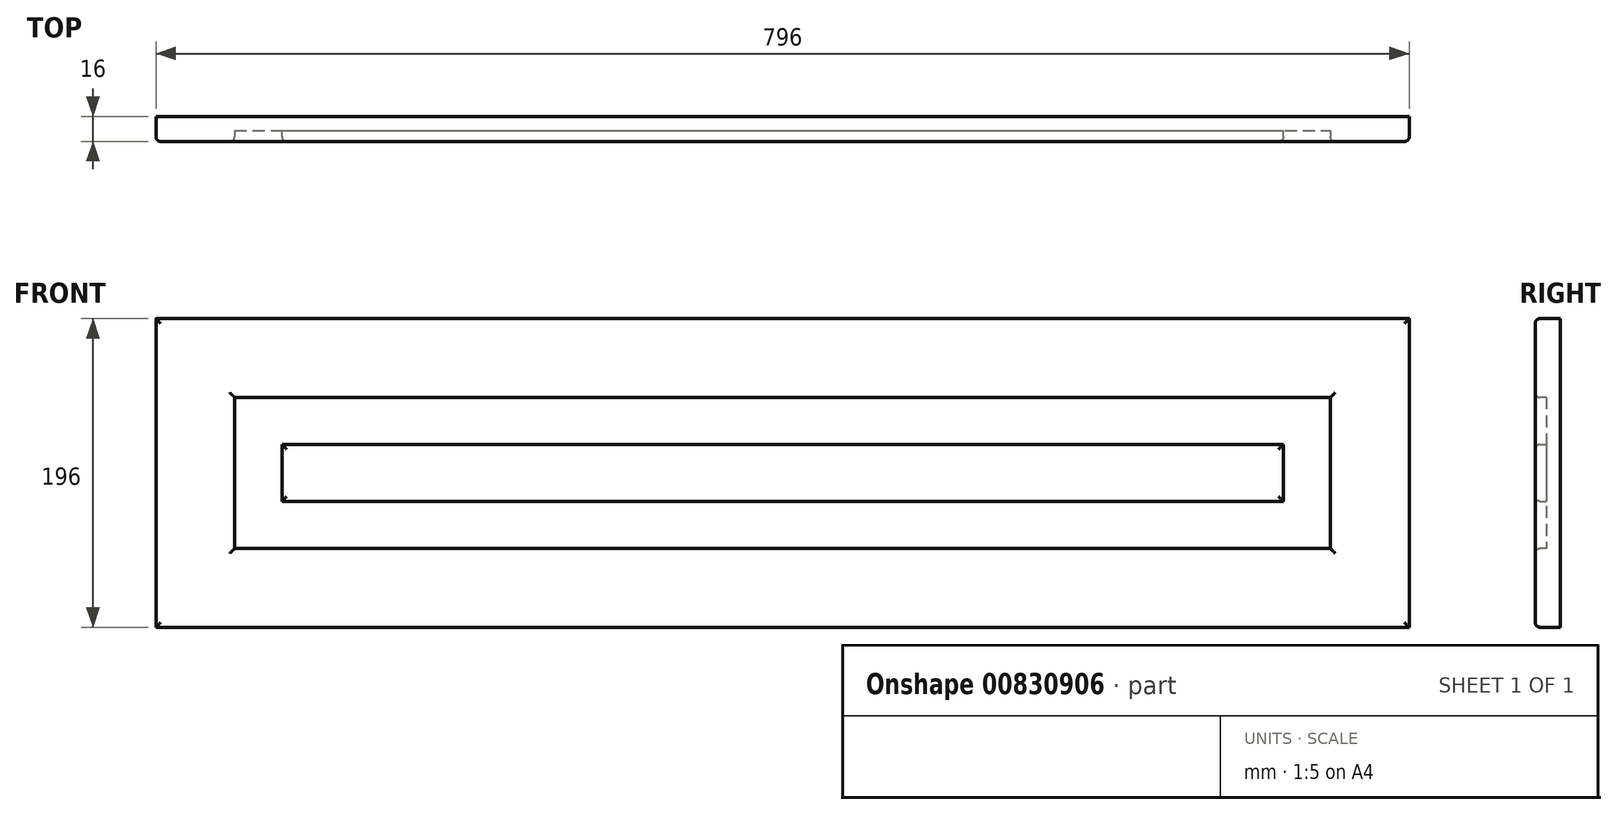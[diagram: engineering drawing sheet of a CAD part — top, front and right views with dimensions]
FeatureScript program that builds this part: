
annotation { "Feature Type Name" : "Feature", "Feature Type Description" : "" }
export const myFeature = defineFeature(function(context is Context, id is Id, definition is map)
    precondition{}
    {
        {
            var Q0;
            Q0=qCreatedBy(makeId("Front.planeOp"),FACE);
            var sketch = newSketch(context, id + "F0", { "sketchPlane" : qUnion([Q0])});
            skLineSegment(sketch, "E0.bottom", {"start": v(0, 0) * mm, "end": v(44.66, 0) * mm});
            skLineSegment(sketch, "E0.top", {"start": v(0, 33.8) * mm, "end": v(44.66, 33.8) * mm});
            skLineSegment(sketch, "E0.left", {"start": v(0, 0) * mm, "end": v(0, 33.8) * mm});
            skLineSegment(sketch, "E0.right", {"start": v(44.66, 0) * mm, "end": v(44.66, 33.8) * mm});
            skSolve(sketch);
        }
        {
            var Q0;
            Q0=makeQuery(id+"F0.imprint","IMPRINT",FACE,{"disambiguationData":[TD([[makeQuery(id+"F0.imprint","IMPRINT",EDGE,{"derivedFrom":sQuery(id+"F0.wireOp",EDGE,"E0.bottom")}),1.0]])]});
            extrude(context, id + "F1", {"entities" : qUnion([Q0]), "depth" : 16 * mm, "offsetDistance" : 25.4 * mm});
        }
        {
            var Q0;
            Q0=makeQuery(id+"F1.opExtrude","SWEPT_FACE",FACE,{"disambiguationData":[OSD([sQuery(id+"F0.wireOp",EDGE,"E0.bottom")])]});
            extrude(context, id + "F2", {"entities" : qUnion([Q0]), "operationType" : NewBodyOperationType.ADD, "oppositeDirection" : true, "depth" : 796 * mm, "offsetDistance" : 25 * mm});
        }
        {
            var Q0;
            {var subQ0=sQuery(id+"F0.wireOp",EDGE,"E0.left");Q0=makeQuery(id+"F2.boolean.opBoolean","MERGE",FACE,{"derivedFrom":[makeQuery(id+"F1.opExtrude","SWEPT_FACE",FACE,{"disambiguationData":[OSD([subQ0])]}),makeQuery(id+"F2.opExtrude","SWEPT_FACE",FACE,{"disambiguationData":[OSD([sQuery(id+"F0.wireOp",EDGE,"E0.bottom"),subQ0])]})]});}
            extrude(context, id + "F3", {"entities" : qUnion([Q0]), "operationType" : NewBodyOperationType.ADD, "oppositeDirection" : true, "depth" : 196 * mm, "offsetDistance" : 25 * mm});
        }
        {
            var Q0;
            {var subQ0=sQuery(id+"F0.wireOp",EDGE,"E0.left");var subQ1=sQuery(id+"F0.wireOp",EDGE,"E0.bottom");Q0=makeQuery(id+"F3.boolean.opBoolean","MERGE",FACE,{"derivedFrom":[makeQuery(id+"F2.boolean.opBoolean","MERGE",FACE,{"derivedFrom":[makeQuery(id+"F1.opExtrude","CAP_FACE",FACE,{"disambiguationData":[OSD([subQ1,sQuery(id+"F0.wireOp",EDGE,"E0.top"),subQ0,sQuery(id+"F0.wireOp",EDGE,"E0.right")])],"isStart":false}),makeQuery(id+"F2.opExtrude","SWEPT_FACE",FACE,{"disambiguationData":[OSD([subQ1]),TDD([makeQuery(id+"F1.opExtrude","CAP_EDGE",EDGE,{"disambiguationData":[OSD([subQ1])],"isStart":false})])]})]}),makeQuery(id+"F3.opExtrude","SWEPT_FACE",FACE,{"disambiguationData":[OSD([subQ1,subQ0]),TDD([makeQuery(id+"F2.boolean.opBoolean","MERGE",EDGE,{"derivedFrom":[makeQuery(id+"F1.opExtrude","CAP_EDGE",EDGE,{"disambiguationData":[OSD([subQ0])],"isStart":false}),makeQuery(id+"F2.opExtrude","SWEPT_EDGE",EDGE,{"disambiguationData":[OSD([subQ1,subQ0]),TDD([makeQuery(id+"F1.opExtrude","CAP_VERTEX",VERTEX,{"disambiguationData":[OSD([subQ1,subQ0])],"isStart":false})])]})]})])]})]});}
            var sketch = newSketch(context, id + "F4", { "sketchPlane" : qUnion([Q0])});
            skLineSegment(sketch, "E1.bottom", {"start": v(59.7, 646.67) * mm, "end": v(128.66, 646.67) * mm});
            skLineSegment(sketch, "E1.top", {"start": v(59.7, 152.97) * mm, "end": v(128.66, 152.97) * mm});
            skLineSegment(sketch, "E1.left", {"start": v(59.7, 646.67) * mm, "end": v(59.7, 152.97) * mm});
            skLineSegment(sketch, "E1.right", {"start": v(128.66, 646.67) * mm, "end": v(128.66, 152.97) * mm});
            skSolve(sketch);
        }
        {
            var Q0;
            Q0=makeQuery(id+"F4.imprint","IMPRINT",FACE,{"disambiguationData":[TD([[makeQuery(id+"F4.imprint","IMPRINT",EDGE,{"derivedFrom":sQuery(id+"F4.wireOp",EDGE,"E1.bottom")}),-1.0]])]});
            extrude(context, id + "F5", {"entities" : qUnion([Q0]), "operationType" : NewBodyOperationType.REMOVE, "oppositeDirection" : true, "depth" : 7 * mm, "offsetDistance" : 25 * mm});
        }
        {
            var Q0;
            Q0=makeQuery(id+"F5.boolean.opBoolean","COPY",FACE,{"derivedFrom":makeQuery(id+"F5.opExtrude","SWEPT_FACE",FACE,{"disambiguationData":[OSD([sQuery(id+"F4.wireOp",EDGE,"E1.left")])]})});
            extrude(context, id + "F6", {"entities" : qUnion([Q0]), "operationType" : NewBodyOperationType.REMOVE, "oppositeDirection" : true, "depth" : 9.7 * mm, "offsetDistance" : 25 * mm});
        }
        {
            var Q0;
            {var subQ0=sQuery(id+"F4.wireOp",EDGE,"E1.bottom");Q0=makeQuery(id+"F6.boolean.opBoolean","MERGE",FACE,{"derivedFrom":[makeQuery(id+"F5.boolean.opBoolean","COPY",FACE,{"derivedFrom":makeQuery(id+"F5.opExtrude","SWEPT_FACE",FACE,{"disambiguationData":[OSD([subQ0])]})}),makeQuery(id+"F6.opExtrude","SWEPT_FACE",FACE,{"disambiguationData":[OSD([subQ0,sQuery(id+"F4.wireOp",EDGE,"E1.left")])]})]});}
            extrude(context, id + "F7", {"entities" : qUnion([Q0]), "operationType" : NewBodyOperationType.ADD, "oppositeDirection" : true, "depth" : 99.33 * mm, "offsetDistance" : 25 * mm});
        }
        {
            var Q0;
            {var subQ0=sQuery(id+"F4.wireOp",EDGE,"E1.bottom");Q0=makeQuery(id+"F6.boolean.opBoolean","MERGE",FACE,{"derivedFrom":[makeQuery(id+"F5.boolean.opBoolean","COPY",FACE,{"derivedFrom":makeQuery(id+"F5.opExtrude","SWEPT_FACE",FACE,{"disambiguationData":[OSD([subQ0])]})}),makeQuery(id+"F6.opExtrude","SWEPT_FACE",FACE,{"disambiguationData":[OSD([subQ0,sQuery(id+"F4.wireOp",EDGE,"E1.left")])]})]});}
            extrude(context, id + "F8", {"entities" : qUnion([Q0]), "operationType" : NewBodyOperationType.REMOVE, "oppositeDirection" : true, "depth" : 99.33 * mm, "offsetDistance" : 25 * mm});
        }
        {
            var Q0;
            {var subQ0=sQuery(id+"F4.wireOp",EDGE,"E1.right");Q0=makeQuery(id+"F8.boolean.opBoolean","MERGE",FACE,{"derivedFrom":[makeQuery(id+"F5.boolean.opBoolean","COPY",FACE,{"derivedFrom":makeQuery(id+"F5.opExtrude","SWEPT_FACE",FACE,{"disambiguationData":[OSD([subQ0])]})}),makeQuery(id+"F8.opExtrude","SWEPT_FACE",FACE,{"disambiguationData":[OSD([sQuery(id+"F4.wireOp",EDGE,"E1.bottom"),subQ0])]})]});}
            extrude(context, id + "F9", {"entities" : qUnion([Q0]), "operationType" : NewBodyOperationType.REMOVE, "oppositeDirection" : true, "depth" : 17.34 * mm, "offsetDistance" : 25 * mm});
        }
        {
            var Q0;
            {var subQ0=sQuery(id+"F4.wireOp",EDGE,"E1.top");Q0=makeQuery(id+"F9.boolean.opBoolean","MERGE",FACE,{"derivedFrom":[makeQuery(id+"F6.boolean.opBoolean","MERGE",FACE,{"derivedFrom":[makeQuery(id+"F5.boolean.opBoolean","COPY",FACE,{"derivedFrom":makeQuery(id+"F5.opExtrude","SWEPT_FACE",FACE,{"disambiguationData":[OSD([subQ0])]})}),makeQuery(id+"F6.opExtrude","SWEPT_FACE",FACE,{"disambiguationData":[OSD([subQ0,sQuery(id+"F4.wireOp",EDGE,"E1.left")])]})]}),makeQuery(id+"F9.opExtrude","SWEPT_FACE",FACE,{"disambiguationData":[OSD([subQ0,sQuery(id+"F4.wireOp",EDGE,"E1.right")])]})]});}
            extrude(context, id + "F10", {"entities" : qUnion([Q0]), "operationType" : NewBodyOperationType.REMOVE, "oppositeDirection" : true, "depth" : 102.97 * mm, "offsetDistance" : 25 * mm});
        }
        {
            var Q0;
            {var subQ0=sQuery(id+"F4.wireOp",EDGE,"E1.right");var subQ1=sQuery(id+"F4.wireOp",EDGE,"E1.top");var subQ2=sQuery(id+"F4.wireOp",EDGE,"E1.left");var subQ3=sQuery(id+"F4.wireOp",EDGE,"E1.bottom");Q0=makeQuery(id+"F10.boolean.opBoolean","MERGE",FACE,{"derivedFrom":[makeQuery(id+"F9.boolean.opBoolean","MERGE",FACE,{"derivedFrom":[makeQuery(id+"F8.boolean.opBoolean","MERGE",FACE,{"derivedFrom":[makeQuery(id+"F6.boolean.opBoolean","MERGE",FACE,{"derivedFrom":[makeQuery(id+"F5.boolean.opBoolean","COPY",FACE,{"derivedFrom":makeQuery(id+"F5.opExtrude","CAP_FACE",FACE,{"disambiguationData":[OSD([subQ3,subQ1,subQ2,subQ0])],"isStart":false})}),makeQuery(id+"F6.opExtrude","SWEPT_FACE",FACE,{"disambiguationData":[OSD([subQ2]),TDD([makeQuery(id+"F5.boolean.opBoolean","COPY",EDGE,{"derivedFrom":makeQuery(id+"F5.opExtrude","CAP_EDGE",EDGE,{"disambiguationData":[OSD([subQ2])],"isStart":false})})])]})]}),makeQuery(id+"F8.opExtrude","SWEPT_FACE",FACE,{"disambiguationData":[OSD([subQ3,subQ2]),TDD([makeQuery(id+"F6.boolean.opBoolean","MERGE",EDGE,{"derivedFrom":[makeQuery(id+"F5.boolean.opBoolean","COPY",EDGE,{"derivedFrom":makeQuery(id+"F5.opExtrude","CAP_EDGE",EDGE,{"disambiguationData":[OSD([subQ3])],"isStart":false})}),makeQuery(id+"F6.opExtrude","SWEPT_EDGE",EDGE,{"disambiguationData":[OSD([subQ3,subQ2]),TDD([makeQuery(id+"F5.boolean.opBoolean","COPY",VERTEX,{"derivedFrom":makeQuery(id+"F5.opExtrude","CAP_VERTEX",VERTEX,{"disambiguationData":[OSD([subQ3,subQ2])],"isStart":false})})])]})]})])]})]}),makeQuery(id+"F9.opExtrude","SWEPT_FACE",FACE,{"disambiguationData":[OSD([subQ3,subQ0]),TDD([makeQuery(id+"F8.boolean.opBoolean","MERGE",EDGE,{"derivedFrom":[makeQuery(id+"F5.boolean.opBoolean","COPY",EDGE,{"derivedFrom":makeQuery(id+"F5.opExtrude","CAP_EDGE",EDGE,{"disambiguationData":[OSD([subQ0])],"isStart":false})}),makeQuery(id+"F8.opExtrude","SWEPT_EDGE",EDGE,{"disambiguationData":[OSD([subQ3,subQ0]),TDD([makeQuery(id+"F5.boolean.opBoolean","COPY",VERTEX,{"derivedFrom":makeQuery(id+"F5.opExtrude","CAP_VERTEX",VERTEX,{"disambiguationData":[OSD([subQ3,subQ0])],"isStart":false})})])]})]})])]})]}),makeQuery(id+"F10.opExtrude","SWEPT_FACE",FACE,{"disambiguationData":[OSD([subQ1,subQ2,subQ0]),TDD([makeQuery(id+"F9.boolean.opBoolean","MERGE",EDGE,{"derivedFrom":[makeQuery(id+"F6.boolean.opBoolean","MERGE",EDGE,{"derivedFrom":[makeQuery(id+"F5.boolean.opBoolean","COPY",EDGE,{"derivedFrom":makeQuery(id+"F5.opExtrude","CAP_EDGE",EDGE,{"disambiguationData":[OSD([subQ1])],"isStart":false})}),makeQuery(id+"F6.opExtrude","SWEPT_EDGE",EDGE,{"disambiguationData":[OSD([subQ1,subQ2]),TDD([makeQuery(id+"F5.boolean.opBoolean","COPY",VERTEX,{"derivedFrom":makeQuery(id+"F5.opExtrude","CAP_VERTEX",VERTEX,{"disambiguationData":[OSD([subQ1,subQ2])],"isStart":false})})])]})]}),makeQuery(id+"F9.opExtrude","SWEPT_EDGE",EDGE,{"disambiguationData":[OSD([subQ1,subQ0]),TDD([makeQuery(id+"F5.boolean.opBoolean","COPY",VERTEX,{"derivedFrom":makeQuery(id+"F5.opExtrude","CAP_VERTEX",VERTEX,{"disambiguationData":[OSD([subQ1,subQ0])],"isStart":false})})])]})]})])]})]});}
            var sketch = newSketch(context, id + "F11", { "sketchPlane" : qUnion([Q0])});
            skLineSegment(sketch, "E2.bottom", {"start": v(74.13, 678.73) * mm, "end": v(109.41, 678.73) * mm});
            skLineSegment(sketch, "E2.top", {"start": v(74.13, 186.63) * mm, "end": v(109.41, 186.63) * mm});
            skLineSegment(sketch, "E2.left", {"start": v(74.13, 678.73) * mm, "end": v(74.13, 186.63) * mm});
            skLineSegment(sketch, "E2.right", {"start": v(109.41, 678.73) * mm, "end": v(109.41, 186.63) * mm});
            skSolve(sketch);
        }
        {
            var Q0;
            Q0=makeQuery(id+"F11.imprint","IMPRINT",FACE,{"disambiguationData":[TD([[makeQuery(id+"F11.imprint","IMPRINT",EDGE,{"derivedFrom":sQuery(id+"F11.wireOp",EDGE,"E2.bottom")}),-1.0]])]});
            extrude(context, id + "F12", {"entities" : qUnion([Q0]), "operationType" : NewBodyOperationType.ADD, "depth" : 7 * mm, "offsetDistance" : 25 * mm});
        }
        {
            var Q0;
            Q0=makeQuery(id+"F12.opExtrude","SWEPT_FACE",FACE,{"disambiguationData":[OSD([sQuery(id+"F11.wireOp",EDGE,"E2.bottom")])]});
            extrude(context, id + "F13", {"entities" : qUnion([Q0]), "operationType" : NewBodyOperationType.ADD, "depth" : 37.27 * mm, "offsetDistance" : 25 * mm});
        }
        {
            var Q0;
            {var subQ0=sQuery(id+"F11.wireOp",EDGE,"E2.right");Q0=makeQuery(id+"F13.boolean.opBoolean","MERGE",FACE,{"derivedFrom":[makeQuery(id+"F12.opExtrude","SWEPT_FACE",FACE,{"disambiguationData":[OSD([subQ0])]}),makeQuery(id+"F13.opExtrude","SWEPT_FACE",FACE,{"disambiguationData":[OSD([sQuery(id+"F11.wireOp",EDGE,"E2.bottom"),subQ0])]})]});}
            extrude(context, id + "F14", {"entities" : qUnion([Q0]), "operationType" : NewBodyOperationType.ADD, "depth" : 6.58 * mm, "offsetDistance" : 25 * mm});
        }
        {
            var Q0;
            {var subQ0=sQuery(id+"F11.wireOp",EDGE,"E2.top");Q0=makeQuery(id+"F14.boolean.opBoolean","MERGE",FACE,{"derivedFrom":[makeQuery(id+"F12.opExtrude","SWEPT_FACE",FACE,{"disambiguationData":[OSD([subQ0])]}),makeQuery(id+"F14.opExtrude","SWEPT_FACE",FACE,{"disambiguationData":[OSD([subQ0,sQuery(id+"F11.wireOp",EDGE,"E2.right")])]})]});}
            extrude(context, id + "F15", {"entities" : qUnion([Q0]), "operationType" : NewBodyOperationType.ADD, "depth" : 106.63 * mm, "offsetDistance" : 25 * mm});
        }
        {
            var Q0;
            {var subQ0=sQuery(id+"F11.wireOp",EDGE,"E2.left");Q0=makeQuery(id+"F15.boolean.opBoolean","MERGE",FACE,{"derivedFrom":[makeQuery(id+"F13.boolean.opBoolean","MERGE",FACE,{"derivedFrom":[makeQuery(id+"F12.opExtrude","SWEPT_FACE",FACE,{"disambiguationData":[OSD([subQ0])]}),makeQuery(id+"F13.opExtrude","SWEPT_FACE",FACE,{"disambiguationData":[OSD([sQuery(id+"F11.wireOp",EDGE,"E2.bottom"),subQ0])]})]}),makeQuery(id+"F15.opExtrude","SWEPT_FACE",FACE,{"disambiguationData":[OSD([sQuery(id+"F11.wireOp",EDGE,"E2.top"),subQ0])]})]});}
            extrude(context, id + "F16", {"entities" : qUnion([Q0]), "operationType" : NewBodyOperationType.REMOVE, "oppositeDirection" : true, "depth" : 5.87 * mm, "offsetDistance" : 25 * mm});
        }
        {
            var Q0;
            Q0=makeQuery(id+"F3.opExtrude","CAP_FACE",FACE,{"disambiguationData":[OSD([sQuery(id+"F0.wireOp",EDGE,"E0.bottom"),sQuery(id+"F0.wireOp",EDGE,"E0.left")])],"isStart":false});
            extrude(context, id + "F17", {"entities" : qUnion([Q0]), "operationType" : NewBodyOperationType.ADD, "depth" : 200 * mm, "offsetDistance" : 25 * mm});
        }
        {
            var Q0;
            {var subQ0=sQuery(id+"F4.wireOp",EDGE,"E1.right");Q0=makeQuery(id+"F10.boolean.opBoolean","MERGE",FACE,{"derivedFrom":[makeQuery(id+"F9.boolean.opBoolean","COPY",FACE,{"derivedFrom":makeQuery(id+"F9.opExtrude","CAP_FACE",FACE,{"disambiguationData":[OSD([sQuery(id+"F4.wireOp",EDGE,"E1.bottom"),subQ0])],"isStart":false})}),makeQuery(id+"F10.opExtrude","SWEPT_FACE",FACE,{"disambiguationData":[OSD([sQuery(id+"F4.wireOp",EDGE,"E1.top"),subQ0])]})]});}
            extrude(context, id + "F18", {"entities" : qUnion([Q0]), "operationType" : NewBodyOperationType.REMOVE, "oppositeDirection" : true, "depth" : 200 * mm, "offsetDistance" : 25 * mm});
        }
        {
            var Q0;
            {var subQ0=sQuery(id+"F11.wireOp",EDGE,"E2.right");var subQ1=sQuery(id+"F11.wireOp",EDGE,"E2.top");Q0=makeQuery(id+"F15.boolean.opBoolean","MERGE",FACE,{"derivedFrom":[makeQuery(id+"F14.opExtrude","CAP_FACE",FACE,{"disambiguationData":[OSD([sQuery(id+"F11.wireOp",EDGE,"E2.bottom"),subQ0])],"isStart":false}),makeQuery(id+"F15.opExtrude","SWEPT_FACE",FACE,{"disambiguationData":[OSD([subQ1,subQ0]),TDD([makeQuery(id+"F14.opExtrude","CAP_EDGE",EDGE,{"disambiguationData":[OSD([subQ1,subQ0])],"isStart":false})])]})]});}
            extrude(context, id + "F19", {"entities" : qUnion([Q0]), "operationType" : NewBodyOperationType.ADD, "depth" : 200 * mm, "offsetDistance" : 25 * mm});
        }
        {
            var Q0;
            Q0=makeQuery(id+"F17.opExtrude","CAP_FACE",FACE,{"disambiguationData":[OSD([sQuery(id+"F0.wireOp",EDGE,"E0.bottom"),sQuery(id+"F0.wireOp",EDGE,"E0.left")])],"isStart":false});
            extrude(context, id + "F20", {"entities" : qUnion([Q0]), "operationType" : NewBodyOperationType.ADD, "depth" : 200 * mm, "offsetDistance" : 25 * mm});
        }
        {
            var Q0;
            Q0=makeQuery(id+"F18.boolean.opBoolean","COPY",FACE,{"derivedFrom":makeQuery(id+"F18.opExtrude","CAP_FACE",FACE,{"disambiguationData":[OSD([sQuery(id+"F4.wireOp",EDGE,"E1.bottom"),sQuery(id+"F4.wireOp",EDGE,"E1.top"),sQuery(id+"F4.wireOp",EDGE,"E1.right")])],"isStart":false})});
            extrude(context, id + "F21", {"entities" : qUnion([Q0]), "operationType" : NewBodyOperationType.REMOVE, "oppositeDirection" : true, "depth" : 200 * mm, "offsetDistance" : 25 * mm});
        }
        {
            var Q0;
            Q0=makeQuery(id+"F19.opExtrude","CAP_FACE",FACE,{"disambiguationData":[OSD([sQuery(id+"F11.wireOp",EDGE,"E2.bottom"),sQuery(id+"F11.wireOp",EDGE,"E2.top"),sQuery(id+"F11.wireOp",EDGE,"E2.right")])],"isStart":false});
            extrude(context, id + "F22", {"entities" : qUnion([Q0]), "operationType" : NewBodyOperationType.ADD, "depth" : 200 * mm, "offsetDistance" : 25 * mm});
        }
        {
            var Q0;
            {var subQ0=sQuery(id+"F11.wireOp",EDGE,"E2.right");var subQ1=sQuery(id+"F11.wireOp",EDGE,"E2.top");Q0=makeQuery(id+"F22.boolean.opBoolean","MERGE",FACE,{"derivedFrom":[makeQuery(id+"F19.boolean.opBoolean","MERGE",FACE,{"derivedFrom":[makeQuery(id+"F15.opExtrude","CAP_FACE",FACE,{"disambiguationData":[OSD([subQ1,subQ0])],"isStart":false}),makeQuery(id+"F19.opExtrude","SWEPT_FACE",FACE,{"disambiguationData":[OSD([subQ1,subQ0])]})]}),makeQuery(id+"F22.opExtrude","SWEPT_FACE",FACE,{"disambiguationData":[OSD([subQ1,subQ0])]})]});}
            extrude(context, id + "F23", {"entities" : qUnion([Q0]), "operationType" : NewBodyOperationType.REMOVE, "oppositeDirection" : true, "depth" : 600 * mm, "offsetDistance" : 25 * mm});
        }
        {
            var Q0;
            {var subQ0=sQuery(id+"F4.wireOp",EDGE,"E1.right");var subQ1=sQuery(id+"F4.wireOp",EDGE,"E1.top");Q0=makeQuery(id+"F21.boolean.opBoolean","MERGE",FACE,{"derivedFrom":[makeQuery(id+"F18.boolean.opBoolean","MERGE",FACE,{"derivedFrom":[makeQuery(id+"F10.boolean.opBoolean","COPY",FACE,{"derivedFrom":makeQuery(id+"F10.opExtrude","CAP_FACE",FACE,{"disambiguationData":[OSD([subQ1,sQuery(id+"F4.wireOp",EDGE,"E1.left"),subQ0])],"isStart":false})}),makeQuery(id+"F18.opExtrude","SWEPT_FACE",FACE,{"disambiguationData":[OSD([subQ1,subQ0])]})]}),makeQuery(id+"F21.opExtrude","SWEPT_FACE",FACE,{"disambiguationData":[OSD([subQ1,subQ0])]})]});}
            extrude(context, id + "F24", {"entities" : qUnion([Q0]), "operationType" : NewBodyOperationType.ADD, "depth" : 600 * mm, "offsetDistance" : 25 * mm});
        }
        {
            var Q0;
            {var subQ0=sQuery(id+"F0.wireOp",EDGE,"E0.left");var subQ1=sQuery(id+"F0.wireOp",EDGE,"E0.bottom");var subQ2=makeQuery(id+"F1.opExtrude","SWEPT_EDGE",EDGE,{"disambiguationData":[OSD([subQ1,subQ0])]});var subQ3=makeQuery(id+"F3.opExtrude","CAP_EDGE",EDGE,{"disambiguationData":[OSD([subQ1,subQ0]),TDD([subQ2])],"isStart":false});Q0=makeQuery(id+"F20.boolean.opBoolean","MERGE",FACE,{"derivedFrom":[makeQuery(id+"F17.boolean.opBoolean","MERGE",FACE,{"derivedFrom":[makeQuery(id+"F3.boolean.opBoolean","MERGE",FACE,{"derivedFrom":[makeQuery(id+"F1.opExtrude","SWEPT_FACE",FACE,{"disambiguationData":[OSD([subQ1])]}),makeQuery(id+"F3.opExtrude","SWEPT_FACE",FACE,{"disambiguationData":[OSD([subQ1,subQ0]),TDD([subQ2])]})]}),makeQuery(id+"F17.opExtrude","SWEPT_FACE",FACE,{"disambiguationData":[OSD([subQ1,subQ0]),TDD([subQ3])]})]}),makeQuery(id+"F20.opExtrude","SWEPT_FACE",FACE,{"disambiguationData":[OSD([subQ1,subQ0]),TDD([makeQuery(id+"F17.opExtrude","CAP_EDGE",EDGE,{"disambiguationData":[OSD([subQ1,subQ0]),TDD([subQ3])],"isStart":false})])]})]});}
            extrude(context, id + "F25", {"entities" : qUnion([Q0]), "operationType" : NewBodyOperationType.REMOVE, "oppositeDirection" : true, "depth" : 600 * mm, "offsetDistance" : 25 * mm});
        }
        {
            var Q0;
            Q0=makeQuery(id+"F25.boolean.opBoolean","COPY",FACE,{"derivedFrom":makeQuery(id+"F25.opExtrude","CAP_FACE",FACE,{"disambiguationData":[OSD([sQuery(id+"F0.wireOp",EDGE,"E0.bottom"),sQuery(id+"F0.wireOp",EDGE,"E0.left")])],"isStart":false})});
            extrude(context, id + "F26", {"entities" : qUnion([Q0]), "operationType" : NewBodyOperationType.ADD, "depth" : 200 * mm, "offsetDistance" : 25 * mm});
        }
        {
            var Q0;
            Q0=makeQuery(id+"F24.opExtrude","CAP_FACE",FACE,{"disambiguationData":[OSD([sQuery(id+"F4.wireOp",EDGE,"E1.top"),sQuery(id+"F4.wireOp",EDGE,"E1.left"),sQuery(id+"F4.wireOp",EDGE,"E1.right")])],"isStart":false});
            extrude(context, id + "F27", {"entities" : qUnion([Q0]), "operationType" : NewBodyOperationType.REMOVE, "oppositeDirection" : true, "depth" : 200 * mm, "offsetDistance" : 25 * mm});
        }
        {
            var Q0;
            Q0=makeQuery(id+"F23.boolean.opBoolean","COPY",FACE,{"derivedFrom":makeQuery(id+"F23.opExtrude","CAP_FACE",FACE,{"disambiguationData":[OSD([sQuery(id+"F11.wireOp",EDGE,"E2.top"),sQuery(id+"F11.wireOp",EDGE,"E2.right")])],"isStart":false})});
            extrude(context, id + "F28", {"entities" : qUnion([Q0]), "operationType" : NewBodyOperationType.ADD, "depth" : 200 * mm, "offsetDistance" : 25 * mm});
        }
        {
            var Q0;
            {var subQ0=sQuery(id+"F0.wireOp",EDGE,"E0.left");var subQ1=sQuery(id+"F0.wireOp",EDGE,"E0.bottom");Q0=makeQuery(id+"F26.boolean.opBoolean","MERGE",FACE,{"derivedFrom":[makeQuery(id+"F20.opExtrude","CAP_FACE",FACE,{"disambiguationData":[OSD([subQ1,subQ0])],"isStart":false}),makeQuery(id+"F26.opExtrude","SWEPT_FACE",FACE,{"disambiguationData":[OSD([subQ1,subQ0]),TDD([makeQuery(id+"F25.boolean.opBoolean","COPY",EDGE,{"derivedFrom":makeQuery(id+"F25.opExtrude","CAP_EDGE",EDGE,{"disambiguationData":[OSD([subQ1,subQ0]),TDD([makeQuery(id+"F20.opExtrude","CAP_EDGE",EDGE,{"disambiguationData":[OSD([subQ1,subQ0]),TDD([makeQuery(id+"F17.opExtrude","CAP_EDGE",EDGE,{"disambiguationData":[OSD([subQ1,subQ0]),TDD([makeQuery(id+"F3.opExtrude","CAP_EDGE",EDGE,{"disambiguationData":[OSD([subQ1,subQ0]),TDD([makeQuery(id+"F1.opExtrude","SWEPT_EDGE",EDGE,{"disambiguationData":[OSD([subQ1,subQ0])]})])],"isStart":false})])],"isStart":false})])],"isStart":false})])],"isStart":false})})])]})]});}
            extrude(context, id + "F29", {"entities" : qUnion([Q0]), "operationType" : NewBodyOperationType.ADD, "depth" : 200 * mm, "offsetDistance" : 25 * mm});
        }
        {
            var Q0;
            {var subQ0=sQuery(id+"F4.wireOp",EDGE,"E1.right");var subQ1=sQuery(id+"F4.wireOp",EDGE,"E1.top");Q0=makeQuery(id+"F27.boolean.opBoolean","MERGE",FACE,{"derivedFrom":[makeQuery(id+"F21.boolean.opBoolean","COPY",FACE,{"derivedFrom":makeQuery(id+"F21.opExtrude","CAP_FACE",FACE,{"disambiguationData":[OSD([sQuery(id+"F4.wireOp",EDGE,"E1.bottom"),subQ1,subQ0])],"isStart":false})}),makeQuery(id+"F27.opExtrude","SWEPT_FACE",FACE,{"disambiguationData":[OSD([subQ1,subQ0])]})]});}
            extrude(context, id + "F30", {"entities" : qUnion([Q0]), "operationType" : NewBodyOperationType.REMOVE, "oppositeDirection" : true, "depth" : 200 * mm, "offsetDistance" : 25 * mm});
        }
        {
            var Q0;
            {var subQ0=sQuery(id+"F11.wireOp",EDGE,"E2.right");var subQ1=sQuery(id+"F11.wireOp",EDGE,"E2.top");Q0=makeQuery(id+"F28.boolean.opBoolean","MERGE",FACE,{"derivedFrom":[makeQuery(id+"F22.opExtrude","CAP_FACE",FACE,{"disambiguationData":[OSD([sQuery(id+"F11.wireOp",EDGE,"E2.bottom"),subQ1,subQ0])],"isStart":false}),makeQuery(id+"F28.opExtrude","SWEPT_FACE",FACE,{"disambiguationData":[OSD([subQ1,subQ0]),TDD([makeQuery(id+"F23.boolean.opBoolean","COPY",EDGE,{"derivedFrom":makeQuery(id+"F23.opExtrude","CAP_EDGE",EDGE,{"disambiguationData":[OSD([subQ1,subQ0]),TDD([makeQuery(id+"F22.opExtrude","CAP_EDGE",EDGE,{"disambiguationData":[OSD([subQ1,subQ0])],"isStart":false})])],"isStart":false})})])]})]});}
            extrude(context, id + "F31", {"entities" : qUnion([Q0]), "operationType" : NewBodyOperationType.ADD, "depth" : 200 * mm, "offsetDistance" : 25 * mm});
        }
        {
            var Q0;
            {var subQ0=sQuery(id+"F11.wireOp",EDGE,"E2.right");var subQ1=sQuery(id+"F11.wireOp",EDGE,"E2.top");Q0=makeQuery(id+"F31.boolean.opBoolean","MERGE",FACE,{"derivedFrom":[makeQuery(id+"F28.opExtrude","CAP_FACE",FACE,{"disambiguationData":[OSD([subQ1,subQ0])],"isStart":false}),makeQuery(id+"F31.opExtrude","SWEPT_FACE",FACE,{"disambiguationData":[OSD([subQ1,subQ0])]})]});}
            extrude(context, id + "F32", {"entities" : qUnion([Q0]), "operationType" : NewBodyOperationType.REMOVE, "oppositeDirection" : true, "depth" : 200 * mm, "offsetDistance" : 25 * mm});
        }
        {
            var Q0;
            {var subQ0=sQuery(id+"F4.wireOp",EDGE,"E1.right");var subQ1=sQuery(id+"F4.wireOp",EDGE,"E1.top");Q0=makeQuery(id+"F30.boolean.opBoolean","MERGE",FACE,{"derivedFrom":[makeQuery(id+"F27.boolean.opBoolean","COPY",FACE,{"derivedFrom":makeQuery(id+"F27.opExtrude","CAP_FACE",FACE,{"disambiguationData":[OSD([subQ1,sQuery(id+"F4.wireOp",EDGE,"E1.left"),subQ0])],"isStart":false})}),makeQuery(id+"F30.opExtrude","SWEPT_FACE",FACE,{"disambiguationData":[OSD([subQ1,subQ0])]})]});}
            extrude(context, id + "F33", {"entities" : qUnion([Q0]), "operationType" : NewBodyOperationType.ADD, "depth" : 200 * mm, "offsetDistance" : 25 * mm});
        }
        {
            var Q0;
            {var subQ0=sQuery(id+"F0.wireOp",EDGE,"E0.left");var subQ1=sQuery(id+"F0.wireOp",EDGE,"E0.bottom");Q0=makeQuery(id+"F29.boolean.opBoolean","MERGE",FACE,{"derivedFrom":[makeQuery(id+"F26.opExtrude","CAP_FACE",FACE,{"disambiguationData":[OSD([subQ1,subQ0])],"isStart":false}),makeQuery(id+"F29.opExtrude","SWEPT_FACE",FACE,{"disambiguationData":[OSD([subQ1,subQ0]),TDD([makeQuery(id+"F26.opExtrude","CAP_EDGE",EDGE,{"disambiguationData":[OSD([subQ1,subQ0]),TDD([makeQuery(id+"F25.boolean.opBoolean","COPY",EDGE,{"derivedFrom":makeQuery(id+"F25.opExtrude","CAP_EDGE",EDGE,{"disambiguationData":[OSD([subQ1,subQ0]),TDD([makeQuery(id+"F20.opExtrude","CAP_EDGE",EDGE,{"disambiguationData":[OSD([subQ1,subQ0]),TDD([makeQuery(id+"F17.opExtrude","CAP_EDGE",EDGE,{"disambiguationData":[OSD([subQ1,subQ0]),TDD([makeQuery(id+"F3.opExtrude","CAP_EDGE",EDGE,{"disambiguationData":[OSD([subQ1,subQ0]),TDD([makeQuery(id+"F1.opExtrude","SWEPT_EDGE",EDGE,{"disambiguationData":[OSD([subQ1,subQ0])]})])],"isStart":false})])],"isStart":false})])],"isStart":false})])],"isStart":false})})])],"isStart":false})])]})]});}
            extrude(context, id + "F34", {"entities" : qUnion([Q0]), "operationType" : NewBodyOperationType.REMOVE, "oppositeDirection" : true, "depth" : 200 * mm, "offsetDistance" : 25 * mm});
        }
        {
            var Q0;
            {var subQ0=sQuery(id+"F4.wireOp",EDGE,"E1.right");var subQ1=sQuery(id+"F4.wireOp",EDGE,"E1.top");var subQ2=makeQuery(id+"F5.boolean.opBoolean","COPY",VERTEX,{"derivedFrom":makeQuery(id+"F5.opExtrude","CAP_VERTEX",VERTEX,{"disambiguationData":[OSD([subQ1,subQ0])],"isStart":true})});var subQ3=makeQuery(id+"F10.boolean.opBoolean","COPY",VERTEX,{"derivedFrom":makeQuery(id+"F10.opExtrude","CAP_VERTEX",VERTEX,{"disambiguationData":[OSD([subQ1,subQ0]),TDD([makeQuery(id+"F9.boolean.opBoolean","COPY",VERTEX,{"derivedFrom":makeQuery(id+"F9.opExtrude","CAP_VERTEX",VERTEX,{"disambiguationData":[OSD([subQ1,subQ0]),TDD([subQ2])],"isStart":false})})])],"isStart":false})});var subQ4=makeQuery(id+"F18.boolean.opBoolean","COPY",VERTEX,{"derivedFrom":makeQuery(id+"F18.opExtrude","CAP_VERTEX",VERTEX,{"disambiguationData":[OSD([subQ1,subQ0]),TDD([subQ3])],"isStart":false})});var subQ5=sQuery(id+"F4.wireOp",EDGE,"E1.left");var subQ6=makeQuery(id+"F21.boolean.opBoolean","MERGE",EDGE,{"derivedFrom":[makeQuery(id+"F18.boolean.opBoolean","MERGE",EDGE,{"derivedFrom":[makeQuery(id+"F10.boolean.opBoolean","COPY",EDGE,{"derivedFrom":makeQuery(id+"F10.opExtrude","CAP_EDGE",EDGE,{"disambiguationData":[OSD([subQ1,subQ5,subQ0]),TDD([makeQuery(id+"F9.boolean.opBoolean","MERGE",EDGE,{"derivedFrom":[makeQuery(id+"F6.boolean.opBoolean","MERGE",EDGE,{"derivedFrom":[makeQuery(id+"F5.boolean.opBoolean","COPY",EDGE,{"derivedFrom":makeQuery(id+"F5.opExtrude","CAP_EDGE",EDGE,{"disambiguationData":[OSD([subQ1])],"isStart":true})}),makeQuery(id+"F6.opExtrude","SWEPT_EDGE",EDGE,{"disambiguationData":[OSD([subQ1,subQ5]),TDD([makeQuery(id+"F5.boolean.opBoolean","COPY",VERTEX,{"derivedFrom":makeQuery(id+"F5.opExtrude","CAP_VERTEX",VERTEX,{"disambiguationData":[OSD([subQ1,subQ5])],"isStart":true})})])]})]}),makeQuery(id+"F9.opExtrude","SWEPT_EDGE",EDGE,{"disambiguationData":[OSD([subQ1,subQ0]),TDD([subQ2])]})]})])],"isStart":false})}),makeQuery(id+"F18.opExtrude","SWEPT_EDGE",EDGE,{"disambiguationData":[OSD([subQ1,subQ0]),TDD([subQ3])]})]}),makeQuery(id+"F21.opExtrude","SWEPT_EDGE",EDGE,{"disambiguationData":[OSD([subQ1,subQ0]),TDD([subQ4])]})]});var subQ7=sQuery(id+"F0.wireOp",EDGE,"E0.left");var subQ8=sQuery(id+"F0.wireOp",EDGE,"E0.bottom");var subQ9=makeQuery(id+"F1.opExtrude","CAP_VERTEX",VERTEX,{"disambiguationData":[OSD([subQ8,subQ7])],"isStart":false});var subQ10=makeQuery(id+"F3.opExtrude","CAP_VERTEX",VERTEX,{"disambiguationData":[OSD([subQ8,subQ7]),TDD([subQ9])],"isStart":false});var subQ11=makeQuery(id+"F17.opExtrude","CAP_VERTEX",VERTEX,{"disambiguationData":[OSD([subQ8,subQ7]),TDD([subQ10])],"isStart":false});var subQ12=makeQuery(id+"F2.boolean.opBoolean","MERGE",EDGE,{"derivedFrom":[makeQuery(id+"F1.opExtrude","CAP_EDGE",EDGE,{"disambiguationData":[OSD([subQ7])],"isStart":false}),makeQuery(id+"F2.opExtrude","SWEPT_EDGE",EDGE,{"disambiguationData":[OSD([subQ8,subQ7]),TDD([subQ9])]})]});var subQ13=makeQuery(id+"F3.opExtrude","CAP_EDGE",EDGE,{"disambiguationData":[OSD([subQ8,subQ7]),TDD([subQ12])],"isStart":false});var subQ14=makeQuery(id+"F17.opExtrude","CAP_EDGE",EDGE,{"disambiguationData":[OSD([subQ8,subQ7]),TDD([subQ13])],"isStart":false});var subQ15=makeQuery(id+"F1.opExtrude","CAP_EDGE",EDGE,{"disambiguationData":[OSD([subQ8])],"isStart":false});Q0=makeQuery(id+"F33.boolean.opBoolean","MERGE",FACE,{"derivedFrom":[makeQuery(id+"F29.boolean.opBoolean","MERGE",FACE,{"derivedFrom":[makeQuery(id+"F26.boolean.opBoolean","MERGE",FACE,{"derivedFrom":[makeQuery(id+"F24.boolean.opBoolean","MERGE",FACE,{"derivedFrom":[makeQuery(id+"F20.boolean.opBoolean","MERGE",FACE,{"derivedFrom":[makeQuery(id+"F17.boolean.opBoolean","MERGE",FACE,{"derivedFrom":[makeQuery(id+"F3.boolean.opBoolean","MERGE",FACE,{"derivedFrom":[makeQuery(id+"F2.boolean.opBoolean","MERGE",FACE,{"derivedFrom":[makeQuery(id+"F1.opExtrude","CAP_FACE",FACE,{"disambiguationData":[OSD([subQ8,sQuery(id+"F0.wireOp",EDGE,"E0.top"),subQ7,sQuery(id+"F0.wireOp",EDGE,"E0.right")])],"isStart":false}),makeQuery(id+"F2.opExtrude","SWEPT_FACE",FACE,{"disambiguationData":[OSD([subQ8]),TDD([subQ15])]})]}),makeQuery(id+"F3.opExtrude","SWEPT_FACE",FACE,{"disambiguationData":[OSD([subQ8,subQ7]),TDD([subQ12])]})]}),makeQuery(id+"F17.opExtrude","SWEPT_FACE",FACE,{"disambiguationData":[OSD([subQ8,subQ7]),TDD([subQ13])]})]}),makeQuery(id+"F20.opExtrude","SWEPT_FACE",FACE,{"disambiguationData":[OSD([subQ8,subQ7]),TDD([subQ14])]})]}),makeQuery(id+"F24.opExtrude","SWEPT_FACE",FACE,{"disambiguationData":[OSD([subQ1,subQ5,subQ0]),TDD([subQ6])]})]}),makeQuery(id+"F26.opExtrude","SWEPT_FACE",FACE,{"disambiguationData":[OSD([subQ8,subQ7]),TDD([makeQuery(id+"F25.boolean.opBoolean","COPY",EDGE,{"derivedFrom":makeQuery(id+"F25.opExtrude","CAP_EDGE",EDGE,{"disambiguationData":[OSD([subQ8,subQ7]),TDD([makeQuery(id+"F20.boolean.opBoolean","MERGE",EDGE,{"derivedFrom":[makeQuery(id+"F17.boolean.opBoolean","MERGE",EDGE,{"derivedFrom":[makeQuery(id+"F3.boolean.opBoolean","MERGE",EDGE,{"derivedFrom":[subQ15,makeQuery(id+"F3.opExtrude","SWEPT_EDGE",EDGE,{"disambiguationData":[OSD([subQ8,subQ7]),TDD([subQ9])]})]}),makeQuery(id+"F17.opExtrude","SWEPT_EDGE",EDGE,{"disambiguationData":[OSD([subQ8,subQ7]),TDD([subQ10])]})]}),makeQuery(id+"F20.opExtrude","SWEPT_EDGE",EDGE,{"disambiguationData":[OSD([subQ8,subQ7]),TDD([subQ11])]})]})])],"isStart":false})})])]})]}),makeQuery(id+"F29.opExtrude","SWEPT_FACE",FACE,{"disambiguationData":[OSD([subQ8,subQ7]),TDD([makeQuery(id+"F26.boolean.opBoolean","MERGE",EDGE,{"derivedFrom":[makeQuery(id+"F20.opExtrude","CAP_EDGE",EDGE,{"disambiguationData":[OSD([subQ8,subQ7]),TDD([subQ14])],"isStart":false}),makeQuery(id+"F26.opExtrude","SWEPT_EDGE",EDGE,{"disambiguationData":[OSD([subQ8,subQ7]),TDD([makeQuery(id+"F25.boolean.opBoolean","COPY",VERTEX,{"derivedFrom":makeQuery(id+"F25.opExtrude","CAP_VERTEX",VERTEX,{"disambiguationData":[OSD([subQ8,subQ7]),TDD([makeQuery(id+"F20.opExtrude","CAP_VERTEX",VERTEX,{"disambiguationData":[OSD([subQ8,subQ7]),TDD([subQ11])],"isStart":false})])],"isStart":false})})])]})]})])]})]}),makeQuery(id+"F33.opExtrude","SWEPT_FACE",FACE,{"disambiguationData":[OSD([subQ1,subQ5,subQ0]),TDD([makeQuery(id+"F30.boolean.opBoolean","MERGE",EDGE,{"derivedFrom":[makeQuery(id+"F27.boolean.opBoolean","COPY",EDGE,{"derivedFrom":makeQuery(id+"F27.opExtrude","CAP_EDGE",EDGE,{"disambiguationData":[OSD([subQ1,subQ5,subQ0]),TDD([makeQuery(id+"F24.opExtrude","CAP_EDGE",EDGE,{"disambiguationData":[OSD([subQ1,subQ5,subQ0]),TDD([subQ6])],"isStart":false})])],"isStart":false})}),makeQuery(id+"F30.opExtrude","SWEPT_EDGE",EDGE,{"disambiguationData":[OSD([subQ1,subQ0]),TDD([makeQuery(id+"F27.boolean.opBoolean","COPY",VERTEX,{"derivedFrom":makeQuery(id+"F27.opExtrude","CAP_VERTEX",VERTEX,{"disambiguationData":[OSD([subQ1,subQ0]),TDD([makeQuery(id+"F24.opExtrude","CAP_VERTEX",VERTEX,{"disambiguationData":[OSD([subQ1,subQ0]),TDD([makeQuery(id+"F21.boolean.opBoolean","COPY",VERTEX,{"derivedFrom":makeQuery(id+"F21.opExtrude","CAP_VERTEX",VERTEX,{"disambiguationData":[OSD([subQ1,subQ0]),TDD([subQ4])],"isStart":false})})])],"isStart":false})])],"isStart":false})})])]})]})])]})]});}
            var Q1;
            {var subQ0=sQuery(id+"F11.wireOp",EDGE,"E2.right");var subQ1=sQuery(id+"F11.wireOp",EDGE,"E2.top");var subQ2=makeQuery(id+"F12.opExtrude","CAP_VERTEX",VERTEX,{"disambiguationData":[OSD([subQ1,subQ0])],"isStart":false});var subQ3=makeQuery(id+"F14.opExtrude","CAP_VERTEX",VERTEX,{"disambiguationData":[OSD([subQ1,subQ0]),TDD([subQ2])],"isStart":false});var subQ4=makeQuery(id+"F15.opExtrude","CAP_VERTEX",VERTEX,{"disambiguationData":[OSD([subQ1,subQ0]),TDD([subQ3])],"isStart":false});var subQ5=makeQuery(id+"F19.opExtrude","CAP_VERTEX",VERTEX,{"disambiguationData":[OSD([subQ1,subQ0]),TDD([subQ4])],"isStart":false});var subQ6=sQuery(id+"F11.wireOp",EDGE,"E2.bottom");var subQ7=makeQuery(id+"F13.boolean.opBoolean","MERGE",EDGE,{"derivedFrom":[makeQuery(id+"F12.opExtrude","CAP_EDGE",EDGE,{"disambiguationData":[OSD([subQ0])],"isStart":false}),makeQuery(id+"F13.opExtrude","SWEPT_EDGE",EDGE,{"disambiguationData":[OSD([subQ6,subQ0]),TDD([makeQuery(id+"F12.opExtrude","CAP_VERTEX",VERTEX,{"disambiguationData":[OSD([subQ6,subQ0])],"isStart":false})])]})]});var subQ8=makeQuery(id+"F15.boolean.opBoolean","MERGE",EDGE,{"derivedFrom":[makeQuery(id+"F14.opExtrude","CAP_EDGE",EDGE,{"disambiguationData":[OSD([subQ6,subQ0]),TDD([subQ7])],"isStart":false}),makeQuery(id+"F15.opExtrude","SWEPT_EDGE",EDGE,{"disambiguationData":[OSD([subQ1,subQ0]),TDD([subQ3])]})]});var subQ9=makeQuery(id+"F19.opExtrude","CAP_EDGE",EDGE,{"disambiguationData":[OSD([subQ6,subQ1,subQ0]),TDD([subQ8])],"isStart":false});var subQ10=makeQuery(id+"F14.boolean.opBoolean","MERGE",EDGE,{"derivedFrom":[makeQuery(id+"F12.opExtrude","CAP_EDGE",EDGE,{"disambiguationData":[OSD([subQ1])],"isStart":false}),makeQuery(id+"F14.opExtrude","SWEPT_EDGE",EDGE,{"disambiguationData":[OSD([subQ1,subQ0]),TDD([subQ2])]})]});Q1=makeQuery(id+"F31.boolean.opBoolean","MERGE",FACE,{"derivedFrom":[makeQuery(id+"F28.boolean.opBoolean","MERGE",FACE,{"derivedFrom":[makeQuery(id+"F22.boolean.opBoolean","MERGE",FACE,{"derivedFrom":[makeQuery(id+"F19.boolean.opBoolean","MERGE",FACE,{"derivedFrom":[makeQuery(id+"F15.boolean.opBoolean","MERGE",FACE,{"derivedFrom":[makeQuery(id+"F14.boolean.opBoolean","MERGE",FACE,{"derivedFrom":[makeQuery(id+"F13.boolean.opBoolean","MERGE",FACE,{"derivedFrom":[makeQuery(id+"F12.opExtrude","CAP_FACE",FACE,{"disambiguationData":[OSD([subQ6,subQ1,sQuery(id+"F11.wireOp",EDGE,"E2.left"),subQ0])],"isStart":false}),makeQuery(id+"F13.opExtrude","SWEPT_FACE",FACE,{"disambiguationData":[OSD([subQ6]),TDD([makeQuery(id+"F12.opExtrude","CAP_EDGE",EDGE,{"disambiguationData":[OSD([subQ6])],"isStart":false})])]})]}),makeQuery(id+"F14.opExtrude","SWEPT_FACE",FACE,{"disambiguationData":[OSD([subQ6,subQ0]),TDD([subQ7])]})]}),makeQuery(id+"F15.opExtrude","SWEPT_FACE",FACE,{"disambiguationData":[OSD([subQ1,subQ0]),TDD([subQ10])]})]}),makeQuery(id+"F19.opExtrude","SWEPT_FACE",FACE,{"disambiguationData":[OSD([subQ6,subQ1,subQ0]),TDD([subQ8])]})]}),makeQuery(id+"F22.opExtrude","SWEPT_FACE",FACE,{"disambiguationData":[OSD([subQ6,subQ1,subQ0]),TDD([subQ9])]})]}),makeQuery(id+"F28.opExtrude","SWEPT_FACE",FACE,{"disambiguationData":[OSD([subQ1,subQ0]),TDD([makeQuery(id+"F23.boolean.opBoolean","COPY",EDGE,{"derivedFrom":makeQuery(id+"F23.opExtrude","CAP_EDGE",EDGE,{"disambiguationData":[OSD([subQ1,subQ0]),TDD([makeQuery(id+"F22.boolean.opBoolean","MERGE",EDGE,{"derivedFrom":[makeQuery(id+"F19.boolean.opBoolean","MERGE",EDGE,{"derivedFrom":[makeQuery(id+"F15.opExtrude","CAP_EDGE",EDGE,{"disambiguationData":[OSD([subQ1,subQ0]),TDD([subQ10])],"isStart":false}),makeQuery(id+"F19.opExtrude","SWEPT_EDGE",EDGE,{"disambiguationData":[OSD([subQ1,subQ0]),TDD([subQ4])]})]}),makeQuery(id+"F22.opExtrude","SWEPT_EDGE",EDGE,{"disambiguationData":[OSD([subQ1,subQ0]),TDD([subQ5])]})]})])],"isStart":false})})])]})]}),makeQuery(id+"F31.opExtrude","SWEPT_FACE",FACE,{"disambiguationData":[OSD([subQ6,subQ1,subQ0]),TDD([makeQuery(id+"F28.boolean.opBoolean","MERGE",EDGE,{"derivedFrom":[makeQuery(id+"F22.opExtrude","CAP_EDGE",EDGE,{"disambiguationData":[OSD([subQ6,subQ1,subQ0]),TDD([subQ9])],"isStart":false}),makeQuery(id+"F28.opExtrude","SWEPT_EDGE",EDGE,{"disambiguationData":[OSD([subQ1,subQ0]),TDD([makeQuery(id+"F23.boolean.opBoolean","COPY",VERTEX,{"derivedFrom":makeQuery(id+"F23.opExtrude","CAP_VERTEX",VERTEX,{"disambiguationData":[OSD([subQ1,subQ0]),TDD([makeQuery(id+"F22.opExtrude","CAP_VERTEX",VERTEX,{"disambiguationData":[OSD([subQ1,subQ0]),TDD([subQ5])],"isStart":false})])],"isStart":false})})])]})]})])]})]});}
            fillet(context, id + "F35", {"entities" : qUnion([Q0, Q1]), "radius" : 3 * mm, "tangentPropagation" : true, "allowEdgeOverflow" : false});
        }
    });
